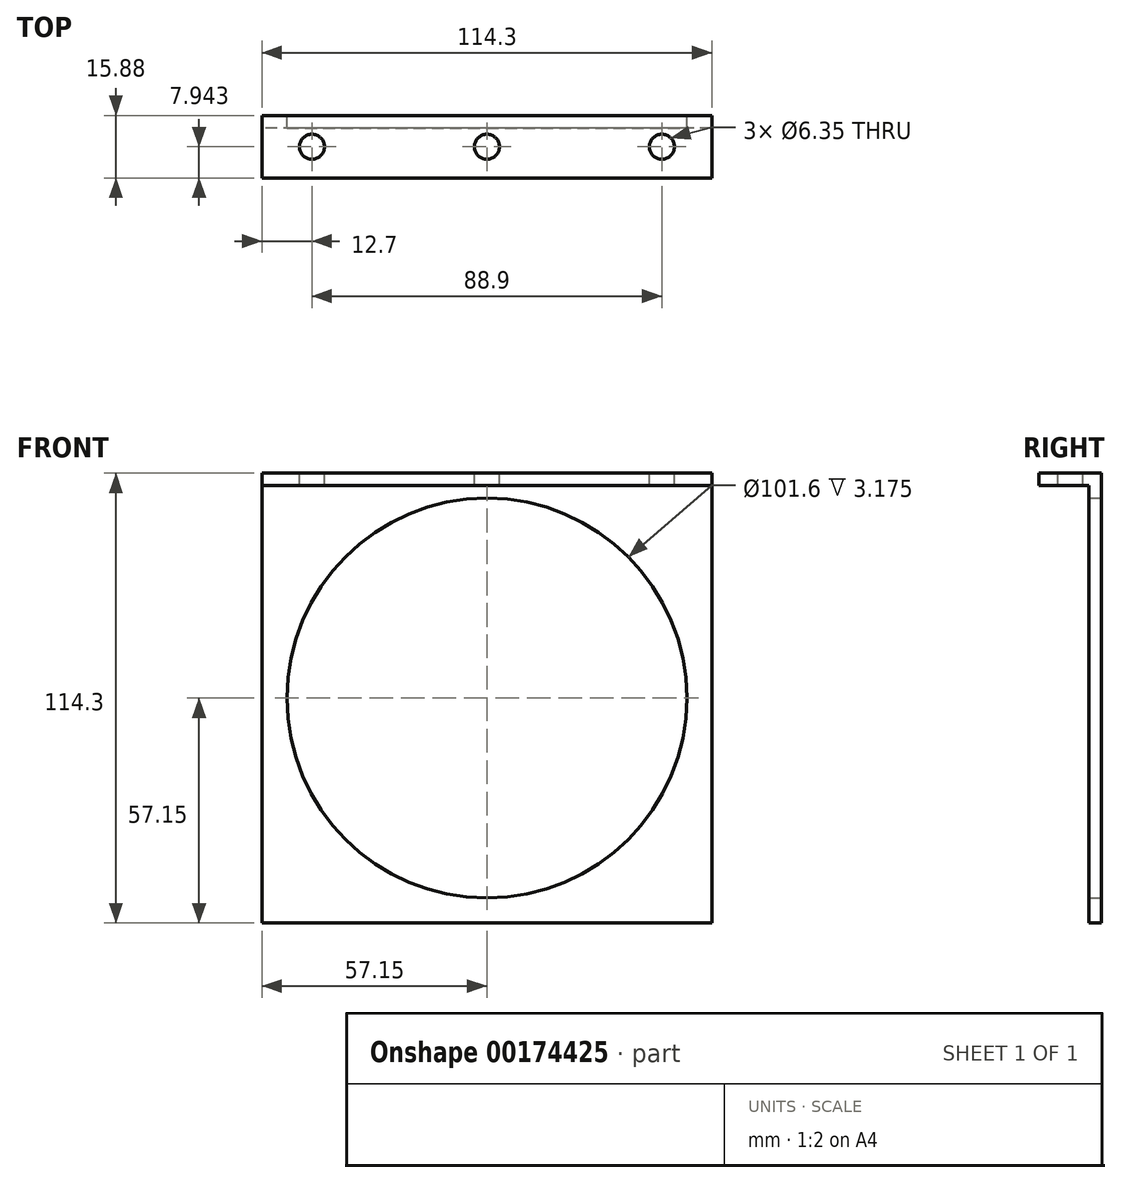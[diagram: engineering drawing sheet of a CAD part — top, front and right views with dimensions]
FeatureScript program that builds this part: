
annotation { "Feature Type Name" : "Feature", "Feature Type Description" : "" }
export const myFeature = defineFeature(function(context is Context, id is Id, definition is map)
    precondition{}
    {
        {
            var Q0;
            Q0=qCreatedBy(makeId("Front.planeOp"),FACE);
            var sketch = newSketch(context, id + "F0", { "sketchPlane" : qUnion([Q0])});
            skLineSegment(sketch, "E0.bottom", {"start": v(57.15, 57.15) * mm, "end": v(-57.15, 57.15) * mm});
            skLineSegment(sketch, "E0.top", {"start": v(57.15, -57.15) * mm, "end": v(-57.15, -57.15) * mm});
            skLineSegment(sketch, "E0.left", {"start": v(57.15, 57.15) * mm, "end": v(57.15, -57.15) * mm});
            skLineSegment(sketch, "E0.right", {"start": v(-57.15, 57.15) * mm, "end": v(-57.15, -57.15) * mm});
            skPoint(sketch, "E0.middle", {"position": v(0, 0) * mm});
            skCircle(sketch, "E1", {"center": v(0, 0) * mm, "radius": 50.8 * mm});
            skSolve(sketch);
        }
        {
            var Q0;
            Q0 = qSketchRegion(id + "F0", true);
            extrude(context, id + "F1", {"entities" : qUnion([Q0]), "depth" : 3.17 * mm});
        }
        {
            var Q0;
            Q0=makeQuery(id+"F1.opExtrude","CAP_FACE",FACE,{"disambiguationData":[OSD([sQuery(id+"F0.wireOp",EDGE,"E0.bottom"),sQuery(id+"F0.wireOp",EDGE,"E0.top"),sQuery(id+"F0.wireOp",EDGE,"E0.left"),sQuery(id+"F0.wireOp",EDGE,"E0.right"),sQuery(id+"F0.wireOp",EDGE,"E1")])],"isStart":false});
            var sketch = newSketch(context, id + "F2", { "sketchPlane" : qUnion([Q0])});
            skLineSegment(sketch, "E2.bottom", {"start": v(-57.15, 57.15) * mm, "end": v(57.15, 57.15) * mm});
            skLineSegment(sketch, "E2.top", {"start": v(-57.15, 53.97) * mm, "end": v(57.15, 53.97) * mm});
            skLineSegment(sketch, "E2.left", {"start": v(-57.15, 57.15) * mm, "end": v(-57.15, 53.97) * mm});
            skLineSegment(sketch, "E2.right", {"start": v(57.15, 57.15) * mm, "end": v(57.15, 53.97) * mm});
            skSolve(sketch);
        }
        {
            var Q0;
            Q0 = qSketchRegion(id + "F2", true);
            extrude(context, id + "F3", {"entities" : qUnion([Q0]), "operationType" : NewBodyOperationType.ADD, "depth" : 12.7 * mm, "offsetDistance" : 25.4 * mm});
        }
        {
            var Q0;
            Q0=makeQuery(id+"F3.boolean.opBoolean","MERGE",FACE,{"derivedFrom":[makeQuery(id+"F1.opExtrude","SWEPT_FACE",FACE,{"disambiguationData":[OSD([sQuery(id+"F0.wireOp",EDGE,"E0.bottom")])]}),makeQuery(id+"F3.opExtrude","SWEPT_FACE",FACE,{"disambiguationData":[OSD([sQuery(id+"F2.wireOp",EDGE,"E2.bottom")])]})]});
            var sketch = newSketch(context, id + "F4", { "sketchPlane" : qUnion([Q0])});
            skLineSegment(sketch, "E3", {"start": v(-57.15, -7.94) * mm, "end": v(57.15, -7.94) * mm});
            skCircle(sketch, "E4", {"center": v(0, -7.94) * mm, "radius": 3.18 * mm});
            skCircle(sketch, "E5", {"center": v(44.45, -7.94) * mm, "radius": 3.18 * mm});
            skCircle(sketch, "E6", {"center": v(-44.45, -7.94) * mm, "radius": 3.18 * mm});
            skSolve(sketch);
        }
        {
            var Q0;
            Q0 = qSketchRegion(id + "F4", true);
            extrude(context, id + "F5", {"entities" : qUnion([Q0]), "operationType" : NewBodyOperationType.REMOVE, "oppositeDirection" : true, "depth" : 25.4 * mm, "offsetDistance" : 25.4 * mm});
        }
    });
